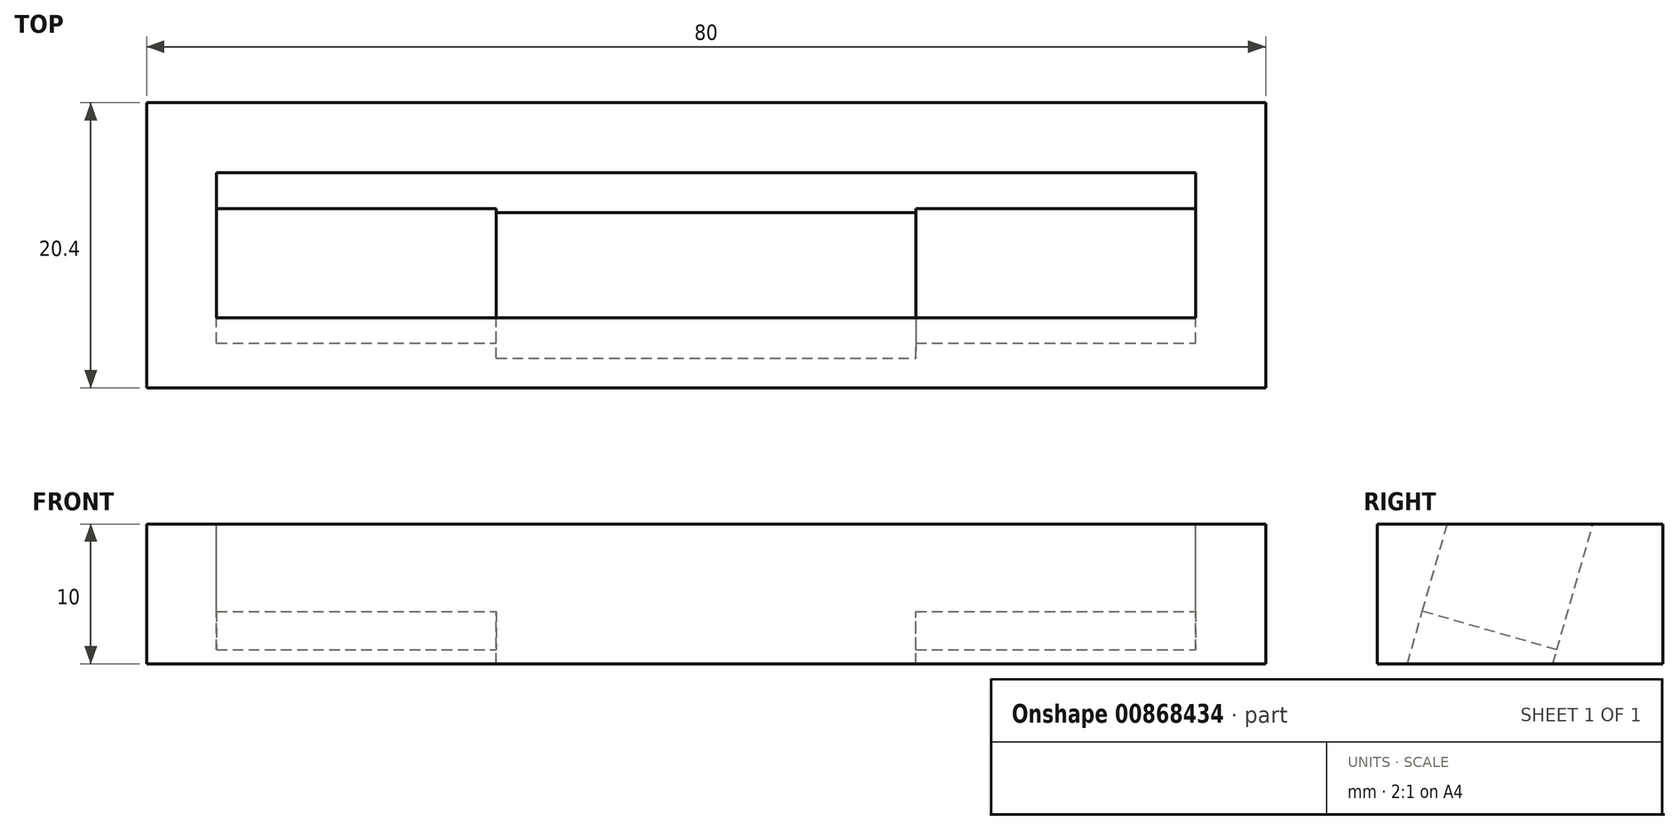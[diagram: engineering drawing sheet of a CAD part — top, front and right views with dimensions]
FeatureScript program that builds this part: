
annotation { "Feature Type Name" : "Feature", "Feature Type Description" : "" }
export const myFeature = defineFeature(function(context is Context, id is Id, definition is map)
    precondition{}
    {
        {
            var Q0;
            Q0=qCreatedBy(makeId("Right.planeOp"),FACE);
            var sketch = newSketch(context, id + "F0", { "sketchPlane" : qUnion([Q0])});
            skLineSegment(sketch, "E0.bottom", {"start": v(-5.53, 0.77) * mm, "end": v(4.08, -1.98) * mm});
            skLineSegment(sketch, "E0.left", {"start": v(-5.53, 0.77) * mm, "end": v(-3.74, 7.02) * mm});
            skLineSegment(sketch, "E0.right", {"start": v(4.08, -1.98) * mm, "end": v(6.66, 7.02) * mm});
            skLineSegment(sketch, "E1", {"start": v(6.66, 7.02) * mm, "end": v(7.66, 7.02) * mm});
            skLineSegment(sketch, "E2", {"start": v(7.66, 7.02) * mm, "end": v(6.66, 7.02) * mm});
            skLineSegment(sketch, "E3", {"start": v(7.66, 7.02) * mm, "end": v(7.66, -2.98) * mm});
            skLineSegment(sketch, "E4.trimOffspring", {"start": v(-3.74, 7.02) * mm, "end": v(-6.53, 7.02) * mm});
            skLineSegment(sketch, "E5", {"start": v(-6.53, 7.02) * mm, "end": v(-6.53, -2.98) * mm});
            skLineSegment(sketch, "E6", {"start": v(7.66, -2.98) * mm, "end": v(-6.53, -2.98) * mm});
            skSolve(sketch);
        }
        {
            var Q0;
            Q0=makeQuery(id+"F0.imprint","IMPRINT",FACE,{"disambiguationData":[TD([[makeQuery(id+"F0.imprint","IMPRINT",EDGE,{"derivedFrom":sQuery(id+"F0.wireOp",EDGE,"E0.bottom")}),-1.0]])]});
            extrude(context, id + "F1", {"entities" : qUnion([Q0]), "endBound" : BoundingType.SYMMETRIC, "oppositeDirection" : true, "depth" : 70 * mm, "offsetDistance" : 25 * mm});
        }
        {
            var Q0;
            Q0=makeQuery(id+"F1.opExtrude","SWEPT_BODY",BODY,{"disambiguationData":[OSD([sQuery(id+"F0.wireOp",EDGE,"E0.bottom"),sQuery(id+"F0.wireOp",EDGE,"E0.left"),sQuery(id+"F0.wireOp",EDGE,"E0.right"),sQuery(id+"F0.wireOp",EDGE,"E1"),sQuery(id+"F0.wireOp",EDGE,"E3"),sQuery(id+"F0.wireOp",EDGE,"E4.trimOffspring"),sQuery(id+"F0.wireOp",EDGE,"E5"),sQuery(id+"F0.wireOp",EDGE,"E6")])]});
            transform(context, id + "F2", {"entities" : qUnion([Q0]), "transformType" : TransformType.TRANSLATION_3D, "dx" : 0 * mm, "dy" : 0 * mm, "dz" : 2.98 * mm, "makeCopy" : false});
        }
        {
            var Q0;
            Q0=makeQuery(id+"F1.opExtrude","CAP_FACE",FACE,{"disambiguationData":[OSD([sQuery(id+"F0.wireOp",EDGE,"E0.bottom"),sQuery(id+"F0.wireOp",EDGE,"E0.left"),sQuery(id+"F0.wireOp",EDGE,"E0.right"),sQuery(id+"F0.wireOp",EDGE,"E1"),sQuery(id+"F0.wireOp",EDGE,"E3"),sQuery(id+"F0.wireOp",EDGE,"E4.trimOffspring"),sQuery(id+"F0.wireOp",EDGE,"E5"),sQuery(id+"F0.wireOp",EDGE,"E6")])],"isStart":false});
            var sketch = newSketch(context, id + "F3", { "sketchPlane" : qUnion([Q0])});
            skLineSegment(sketch, "E7.bottom", {"start": v(-7.66, 10) * mm, "end": v(6.53, 10) * mm});
            skLineSegment(sketch, "E7.top", {"start": v(-7.66, 0) * mm, "end": v(6.53, 0) * mm});
            skLineSegment(sketch, "E7.left", {"start": v(-7.66, 10) * mm, "end": v(-7.66, 0) * mm});
            skLineSegment(sketch, "E7.right", {"start": v(6.53, 10) * mm, "end": v(6.53, 0) * mm});
            skSolve(sketch);
        }
        {
            var Q0;
            Q0=qSketchRegion(id+"F3",true);
            extrude(context, id + "F4", {"entities" : qUnion([Q0]), "operationType" : NewBodyOperationType.ADD, "depth" : 5 * mm, "offsetDistance" : 25 * mm});
        }
        {
            var Q0;
            Q0=makeQuery(id+"F1.opExtrude","CAP_FACE",FACE,{"disambiguationData":[OSD([sQuery(id+"F0.wireOp",EDGE,"E0.bottom"),sQuery(id+"F0.wireOp",EDGE,"E0.left"),sQuery(id+"F0.wireOp",EDGE,"E0.right"),sQuery(id+"F0.wireOp",EDGE,"E1"),sQuery(id+"F0.wireOp",EDGE,"E3"),sQuery(id+"F0.wireOp",EDGE,"E4.trimOffspring"),sQuery(id+"F0.wireOp",EDGE,"E5"),sQuery(id+"F0.wireOp",EDGE,"E6")])],"isStart":true});
            var sketch = newSketch(context, id + "F5", { "sketchPlane" : qUnion([Q0])});
            skLineSegment(sketch, "E8.bottom", {"start": v(-6.53, 10) * mm, "end": v(7.66, 10) * mm});
            skLineSegment(sketch, "E8.top", {"start": v(-6.53, 0) * mm, "end": v(7.66, 0) * mm});
            skLineSegment(sketch, "E8.left", {"start": v(-6.53, 10) * mm, "end": v(-6.53, 0) * mm});
            skLineSegment(sketch, "E8.right", {"start": v(7.66, 10) * mm, "end": v(7.66, 0) * mm});
            skSolve(sketch);
        }
        {
            var Q0;
            Q0=makeQuery(id+"F5.imprint","IMPRINT",FACE,{"disambiguationData":[TD([[makeQuery(id+"F5.imprint","IMPRINT",EDGE,{"derivedFrom":sQuery(id+"F5.wireOp",EDGE,"E8.top")}),-1.0]])]});
            var Q1;
            Q1=makeQuery(id+"F5.imprint","IMPRINT",FACE,{"disambiguationData":[TD([[makeQuery(id+"F5.imprint","IMPRINT",EDGE,{"derivedFrom":makeQuery(id+"F1.opExtrude","CAP_EDGE",EDGE,{"disambiguationData":[OSD([sQuery(id+"F0.wireOp",EDGE,"E0.bottom")])],"isStart":true})}),1.0]])]});
            extrude(context, id + "F6", {"entities" : qUnion([Q0, Q1]), "operationType" : NewBodyOperationType.ADD, "depth" : 5 * mm, "offsetDistance" : 25 * mm});
        }
        {
            var Q0;
            Q0=makeQuery(id+"F1.opExtrude","SWEPT_FACE",FACE,{"disambiguationData":[OSD([sQuery(id+"F0.wireOp",EDGE,"E0.bottom")])]});
            var sketch = newSketch(context, id + "F7", { "sketchPlane" : qUnion([Q0])});
            skLineSegment(sketch, "E9", {"start": v(0, 3.64) * mm, "end": v(15, 3.64) * mm});
            skLineSegment(sketch, "E10", {"start": v(15, 3.64) * mm, "end": v(15, -6.36) * mm});
            skLineSegment(sketch, "E11", {"start": v(15, -6.36) * mm, "end": v(-15, -6.36) * mm});
            skLineSegment(sketch, "E12", {"start": v(-15, -6.36) * mm, "end": v(-15, 3.64) * mm});
            skLineSegment(sketch, "E13", {"start": v(-15, 3.64) * mm, "end": v(0, 3.64) * mm});
            skSolve(sketch);
        }
        {
            var Q0;
            Q0=makeQuery(id+"F6.boolean.opBoolean","MERGE",FACE,{"derivedFrom":[makeQuery(id+"F4.boolean.opBoolean","MERGE",FACE,{"derivedFrom":[makeQuery(id+"F1.opExtrude","SWEPT_FACE",FACE,{"disambiguationData":[OSD([sQuery(id+"F0.wireOp",EDGE,"E5")])]}),makeQuery(id+"F4.opExtrude","SWEPT_FACE",FACE,{"disambiguationData":[OSD([sQuery(id+"F3.wireOp",EDGE,"E7.right")])]})]}),makeQuery(id+"F6.opExtrude","SWEPT_FACE",FACE,{"disambiguationData":[OSD([sQuery(id+"F5.wireOp",EDGE,"E8.left")])]})]});
            extrude(context, id + "F8", {"entities" : qUnion([Q0]), "operationType" : NewBodyOperationType.ADD, "depth" : 0.5 * mm, "offsetDistance" : 25 * mm});
        }
        {
            var Q0;
            Q0=makeQuery(id+"F7.imprint","IMPRINT",FACE,{"disambiguationData":[TD([[makeQuery(id+"F7.imprint","IMPRINT",EDGE,{"derivedFrom":sQuery(id+"F7.wireOp",EDGE,"E9")}),-1.0]])]});
            extrude(context, id + "F9", {"entities" : qUnion([Q0]), "operationType" : NewBodyOperationType.REMOVE, "oppositeDirection" : true, "depth" : 200 * mm, "offsetDistance" : 25 * mm});
        }
        {
            var Q0;
            Q0=makeQuery(id+"F8.opExtrude","CAP_FACE",FACE,{"disambiguationData":[OSD([sQuery(id+"F0.wireOp",EDGE,"E5"),sQuery(id+"F3.wireOp",EDGE,"E7.right"),sQuery(id+"F5.wireOp",EDGE,"E8.left")])],"isStart":false});
            extrude(context, id + "F10", {"entities" : qUnion([Q0]), "operationType" : NewBodyOperationType.ADD, "depth" : 1.71 * mm, "offsetDistance" : 25 * mm});
        }
        {
            var Q0;
            Q0=makeQuery(id+"F6.boolean.opBoolean","MERGE",FACE,{"derivedFrom":[makeQuery(id+"F4.boolean.opBoolean","MERGE",FACE,{"derivedFrom":[makeQuery(id+"F1.opExtrude","SWEPT_FACE",FACE,{"disambiguationData":[OSD([sQuery(id+"F0.wireOp",EDGE,"E3")])]}),makeQuery(id+"F4.opExtrude","SWEPT_FACE",FACE,{"disambiguationData":[OSD([sQuery(id+"F3.wireOp",EDGE,"E7.left")])]})]}),makeQuery(id+"F6.opExtrude","SWEPT_FACE",FACE,{"disambiguationData":[OSD([sQuery(id+"F5.wireOp",EDGE,"E8.right")])]})]});
            extrude(context, id + "F11", {"entities" : qUnion([Q0]), "operationType" : NewBodyOperationType.ADD, "depth" : 4 * mm, "offsetDistance" : 25 * mm});
        }
    });
